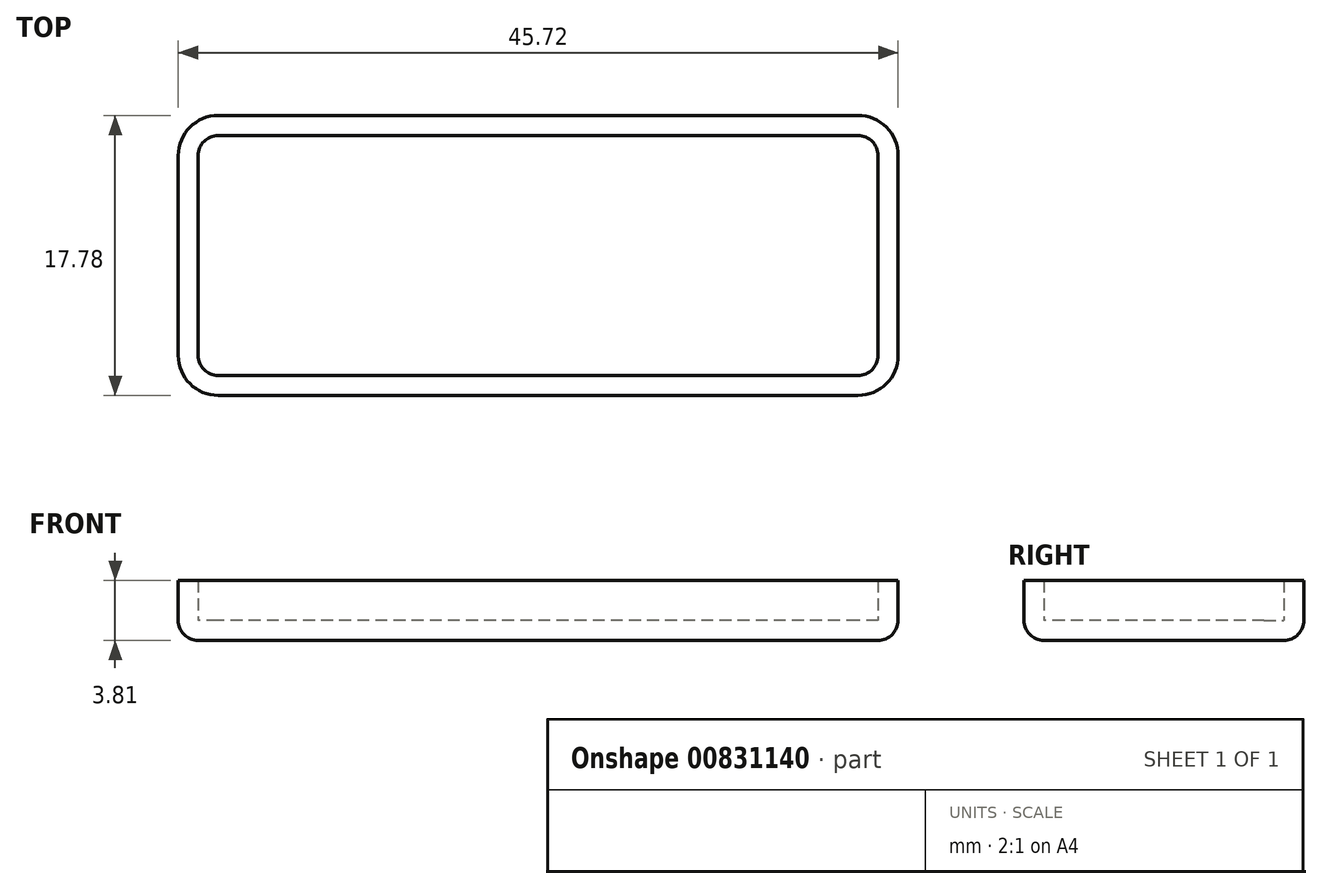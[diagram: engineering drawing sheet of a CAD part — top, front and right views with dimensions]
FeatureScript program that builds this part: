
annotation { "Feature Type Name" : "Feature", "Feature Type Description" : "" }
export const myFeature = defineFeature(function(context is Context, id is Id, definition is map)
    precondition{}
    {
        {
            var Q0;
            Q0=qCreatedBy(makeId("Top.planeOp"),FACE);
            var sketch = newSketch(context, id + "F0", { "sketchPlane" : qUnion([Q0])});
            skLineSegment(sketch, "E0.bottom", {"start": v(20.32, 8.9) * mm, "end": v(-20.32, 8.9) * mm});
            skLineSegment(sketch, "E0.top", {"start": v(20.32, -8.9) * mm, "end": v(-20.32, -8.9) * mm});
            skLineSegment(sketch, "E0.left", {"start": v(22.86, 6.35) * mm, "end": v(22.86, -6.35) * mm});
            skLineSegment(sketch, "E0.right", {"start": v(-22.86, 6.35) * mm, "end": v(-22.86, -6.35) * mm});
            skPoint(sketch, "E0.middle", {"position": v(0, 0) * mm});
            skPoint(sketch, "E1.visualSharp", {"position": v(-22.86, 8.9) * mm});
            skArc(sketch, "E1.filletArc", {"start": v(-20.32, 8.9) * mm, "mid": v(-22.12, 8.15) * mm, "end": v(-22.86, 6.35) * mm});
            skPoint(sketch, "E2.visualSharp", {"position": v(22.86, 8.9) * mm});
            skArc(sketch, "E2.filletArc", {"start": v(22.86, 6.35) * mm, "mid": v(22.12, 8.15) * mm, "end": v(20.32, 8.9) * mm});
            skPoint(sketch, "E3.visualSharp", {"position": v(22.86, -8.9) * mm});
            skArc(sketch, "E3.filletArc", {"start": v(20.32, -8.9) * mm, "mid": v(22.12, -8.15) * mm, "end": v(22.86, -6.35) * mm});
            skPoint(sketch, "E4.visualSharp", {"position": v(-22.86, -8.9) * mm});
            skArc(sketch, "E4.filletArc", {"start": v(-22.86, -6.35) * mm, "mid": v(-22.12, -8.15) * mm, "end": v(-20.32, -8.9) * mm});
            skSolve(sketch);
        }
        {
            var Q0;
            Q0=makeQuery(id+"F0.imprint","IMPRINT",FACE,{"disambiguationData":[TD([[makeQuery(id+"F0.imprint","IMPRINT",EDGE,{"derivedFrom":sQuery(id+"F0.wireOp",EDGE,"E0.bottom")}),1.0]])]});
            extrude(context, id + "F1", {"entities" : qUnion([Q0]), "depth" : 3.8 * mm, "offsetDistance" : 25.4 * mm});
        }
        {
            var Q0;
            Q0=makeQuery(id+"F1.opExtrude","CAP_FACE",FACE,{"disambiguationData":[OSD([sQuery(id+"F0.wireOp",EDGE,"E0.bottom"),sQuery(id+"F0.wireOp",EDGE,"E0.top"),sQuery(id+"F0.wireOp",EDGE,"E0.left"),sQuery(id+"F0.wireOp",EDGE,"E0.right"),sQuery(id+"F0.wireOp",EDGE,"E1.filletArc"),sQuery(id+"F0.wireOp",EDGE,"E2.filletArc"),sQuery(id+"F0.wireOp",EDGE,"E3.filletArc"),sQuery(id+"F0.wireOp",EDGE,"E4.filletArc")])],"isStart":false});
            shell(context, id + "F2", {"entities" : qUnion([Q0]), "thickness" : 1.27 * mm});
        }
        {
            var Q0;
            Q0=makeQuery(id+"F1.opExtrude","CAP_EDGE",EDGE,{"disambiguationData":[OSD([sQuery(id+"F0.wireOp",EDGE,"E0.top")])],"isStart":true});
            fillet(context, id + "F3", {"entities" : qUnion([Q0]), "radius" : 1.27 * mm, "tangentPropagation" : true, "allowEdgeOverflow" : false});
        }
    });
